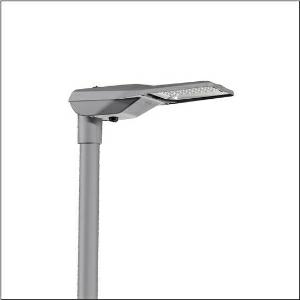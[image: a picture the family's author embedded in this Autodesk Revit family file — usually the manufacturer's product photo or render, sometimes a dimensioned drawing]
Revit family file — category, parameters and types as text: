
# Revit family: streetlight_sl_21_iq_mini___st1_0a_5xe2d51y08hb_d8f2
name_source: partatom
category: Lighting Fixtures
units: mm (PartAtom-declared; Revit-internal decimal feet)

## family parameters
Cut with Voids When Loaded = No
Host = Face
Light Source = No
Part Type = Normal
Room Calculation Point = No
Round Connector Dimension = Use Diameter
Shared = No

## types (1)
- --- (1 x LED, 8560 lm, 71 W, 3000K)
    Apparent Load = 71 VA
    CIE Flux Codes = 37 72 97 100 100
    Color Rendering = 80
    Color Temperature = 3000K
    Default Elevation = 1800 mm
    Description = Streetlight SL 21 iQ mini, mast luminaire, primary light control with lens, of PMMA, primary optical cover: cover, of toughened safety glass, transparent, light distribution: ST1.0a, light emission: direct distribution, primary light characteristic: asymmetric, installation type: post-top, side-entry, LED, High Power LED, rated luminous flux: 8.560lm, luminous efficacy: 121lm/W, light colour: 830, colour temperature: 3000K, control gear: iQ-Street Remote, D4i with power reduction, control: pre-setting: logarithmic dimming characteristic, Street-Remote, Auto-Match, Temp-Guard, Lumen-Switch, Night-Set, Smart-Wire, Light-Fading, Desk-Remote (wireless, voltage-free reading and setting of iQ features in the workshop via application-optimized NFC function/RFID function), optimised constant luminous flux control (CLO 2.0), mains connection: 220..240V, AC, 50/60Hz, start of lifetime: 71W, end of service life: 75W, reduction: 30W, luminaire housing, of diecast aluminium, powder-coated, Siteco® metallic grey (DB 702S), corrosivity category C5 mid according to DIN EN ISO 12944, please order mast flange separately, inclination adjustable: 0°, 5°, 10°, 15°, sealing non-destructively replaceable, multi-level sealing system, length: 628mm, width: 235mm, height: 110mm, mast flange for spigot size: 42mm (side-entry): 5XC10008XM4, 60/48mm (side-entry/post-top): 5XC10108XM2, 76/60mm (side-entry/post-top): 5XC10108XM1, mounting height: 4..8m, Smart Interface below and above, protection rating (complete): IP66, insulation class (complete): insulation class II (safety insulation), certification: CE, ENEC, ENEC+, VDE, impact resistance: IK10, permissible operating ambient temperature for outdoor applications: -40..+50°C, standard-compliant lighting for roads and squares, packaging unit: 1 piece

Light Distribution: ST1.0a
    Height = 110 mm
    Lamp = 1 x LED
    Lamp Light Flux = 8560 lm
    Lamp Power = 71 W
    Lamp count = 1
    Length = 625 mm
    Luminous efficacy = 121 lm/W
    Manufacturer = Siteco
    ModVariant = No
    Model = 5XE2D51Y08HB
    Number of Poles = 1
    OnlyDefault = Yes
    Power Factor = 1
    Product Name = Streetlight SL 21 iQ mini | ST1.0a
    Product group = mast luminaire | pylon top
    ProductGroupID = 6100
    Protection Class = Protection class II
    Protection Degree = IP 66
    RLX_Detail_Level = 1
    RLX_Emergency_Light_Flux = 0 lm
    RLX_Emergency_Type = 0
    RLX_Emergency_Type_DB = No
    RlxData = <blob elided: 26589 chars, md5=5282680d>
    Socket = socket
    Standby Power = 0 W
    System Light Flux = 8560 lm
    System Power = 71 W
    Type Comments = factory setting: luminous flux: 100 % | dim-lin: 254 | 716 mA
    Type Image = l_1003514.jpg
    URL = http://relux.com
    VarID = @adj_114798
    Voltage = 0 V
    Weight = 0.00 kg
    Width = 234 mm

## geometry (parser evidence)
native form markers: Blend x4, Sweep x9
no freeform markers — native parametric forms only
